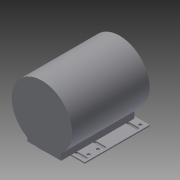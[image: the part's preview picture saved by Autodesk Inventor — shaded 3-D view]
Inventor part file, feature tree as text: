
AUTODESK INVENTOR PART (.ipt)
format: ipt  version: 2016 (Build 200138000, 138)  size: 213,504 bytes
history: native  units: in
note: dims shown in document units (in); Inventor stores cm internally (conversion verified against a paired STEP export)
features: sketch x7, extrude x5, plane x3, hole x1, projected_geometry x1
ambient origin geometry x8: Origin, YZ Plane, XZ Plane, XY Plane, X Axis, Y Axis, Z Axis, Center Point
bodies: Solid1 (feature_tree)
feature tree (17):
  extrude  "Extrusion1"  Depth=0.1in
  extrude  "Extrusion2"  Depth=2.0in
  hole  "Hole1"  [1 undecoded]
  plane  "Work Plane2"
  extrude  "Extrusion3"  TaperAngle=0.0deg  [1 undecoded]
  plane  "Work Plane7"
  extrude  "Extrusion4"  TaperAngle=45.0deg  [1 undecoded]
  plane  "Work Plane9"
  extrude  "Extrusion5"  TaperAngle=135.0deg  [1 undecoded]
  sketch  "Sketch7"  dims[d12=135.0deg d13=0.196in d14=0.5in d15=0.375in d16=0.25in d17=0.5635in d18=0.75in d19=0.8108in d20=7.877in d21=0.25in d22=3.65in d23=1.0in d24=0.0in d27=0.206in d28=0.0in d29=0.125in d30=0.0in d31=0.333in d38=0.333in d39=0.333in d40=0.902in d41=0.333in d51=0.3365in d52=0.25in d53=0.0in d54=7.0in d55=6.5in d56=2.003in d57=0.503in d58=0.266in d59=0.503in d60=3.564in d62=0.367in]
  sketch  "Sketch1"  dims[d0=0.625in d1=0.1in]
  sketch  "Sketch2"  dims[d2=0.191in d3=2.0in]
  sketch  "Sketch3"  dims[d4=0.0in d5=6.5in]
  sketch  "Sketch4"  dims[d6=8.377in d7=0.0in]
  projected_geometry  "Projected Loop1"
  sketch  "Sketch5"  dims[d8=5.75in d9=45.0deg]
  sketch  "Sketch6"  dims[d10=45.0deg d11=135.0deg]
note: 4 required parameter values undecoded (feature->parameter linkage not recoverable at this tier; creation-order binding heuristic only, values carry confidence <= 0.55)
